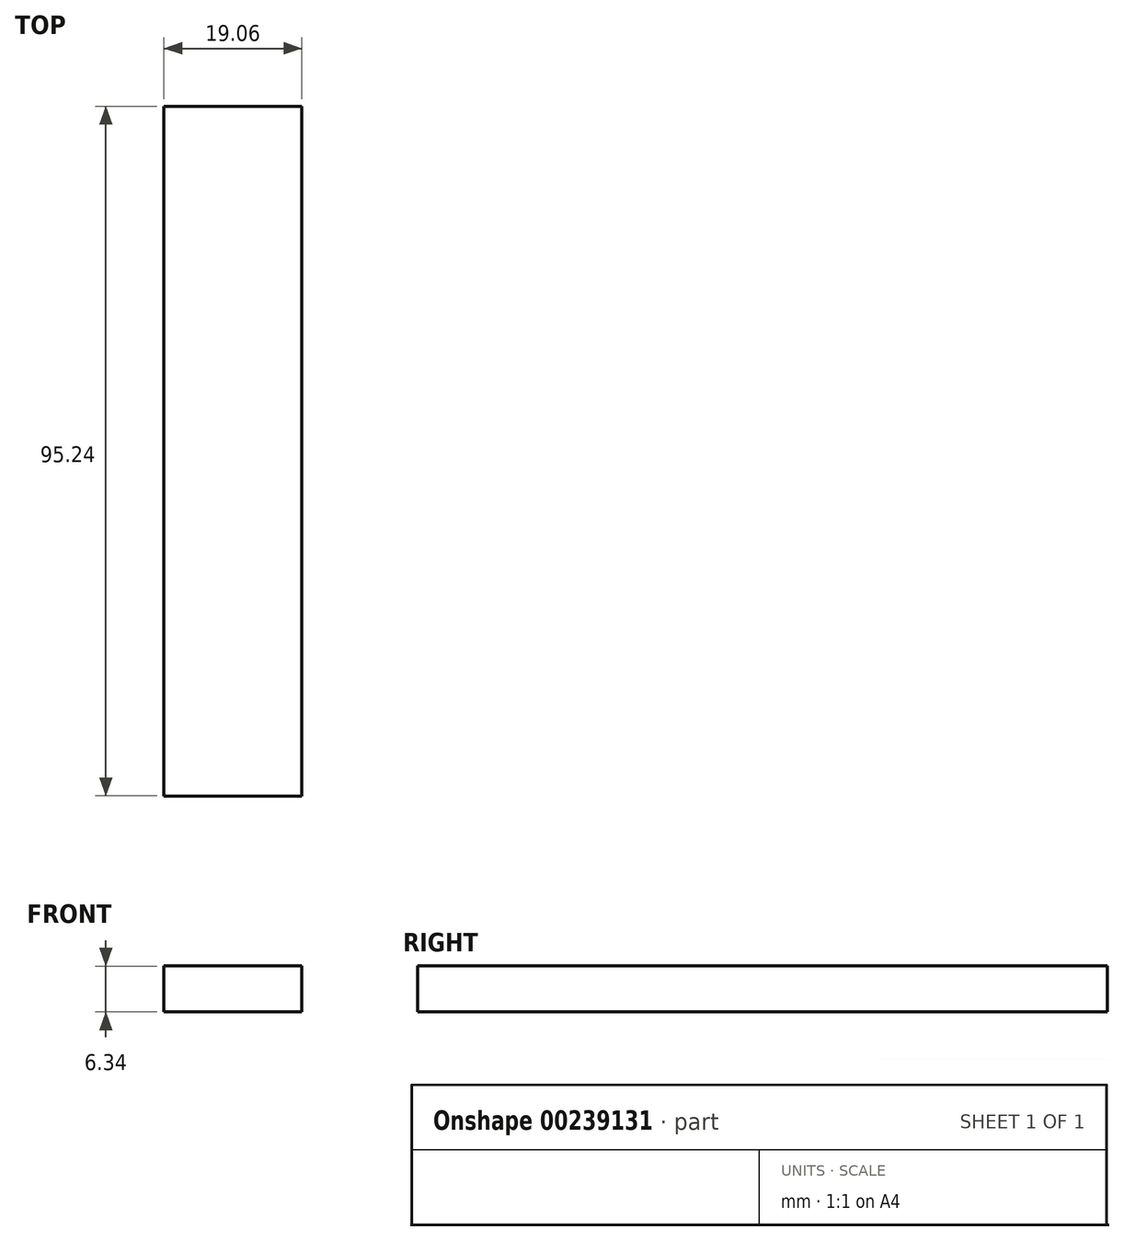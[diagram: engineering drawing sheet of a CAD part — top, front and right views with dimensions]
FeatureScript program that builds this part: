
annotation { "Feature Type Name" : "Feature", "Feature Type Description" : "" }
export const myFeature = defineFeature(function(context is Context, id is Id, definition is map)
    precondition{}
    {
        {
            var Q0;
            Q0=qCreatedBy(makeId("Front.planeOp"),FACE);
            var sketch = newSketch(context, id + "F0", { "sketchPlane" : qUnion([Q0])});
            skLineSegment(sketch, "E0.bottom", {"start": v(-9.52, 3.17) * mm, "end": v(9.52, 3.17) * mm});
            skLineSegment(sketch, "E0.top", {"start": v(-9.52, -3.18) * mm, "end": v(9.52, -3.18) * mm});
            skLineSegment(sketch, "E0.left", {"start": v(-9.52, 3.17) * mm, "end": v(-9.53, -3.18) * mm});
            skLineSegment(sketch, "E0.right", {"start": v(9.52, 3.17) * mm, "end": v(9.52, -3.18) * mm});
            skPoint(sketch, "E0.middle", {"position": v(0, 0) * mm});
            skSolve(sketch);
        }
        {
            var Q0;
            Q0=makeQuery(id+"F0.imprint","IMPRINT",FACE,{"disambiguationData":[TD([[makeQuery(id+"F0.imprint","IMPRINT",EDGE,{"derivedFrom":sQuery(id+"F0.wireOp",EDGE,"E0.bottom")}),-1.0]])]});
            extrude(context, id + "F1", {"entities" : qUnion([Q0]), "endBound" : BoundingType.SYMMETRIC, "depth" : 95.25 * mm});
        }
    });
